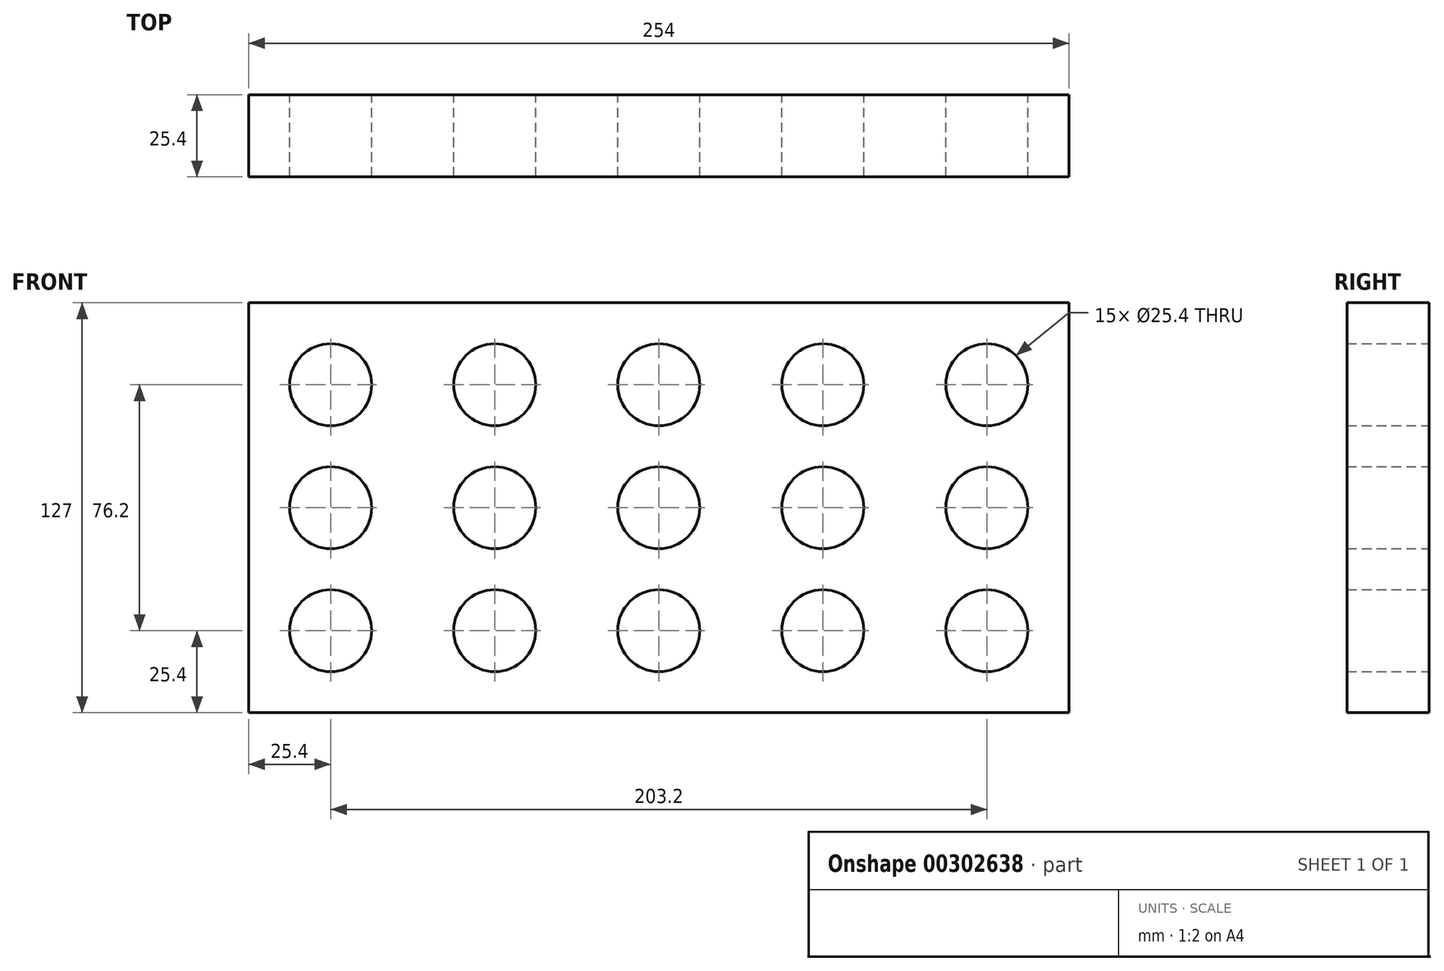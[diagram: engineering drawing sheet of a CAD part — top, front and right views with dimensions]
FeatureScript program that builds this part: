
annotation { "Feature Type Name" : "Feature", "Feature Type Description" : "" }
export const myFeature = defineFeature(function(context is Context, id is Id, definition is map)
    precondition{}
    {
        {
            var Q0;
            Q0=qCreatedBy(makeId("Front.planeOp"),FACE);
            var sketch = newSketch(context, id + "F0", { "sketchPlane" : qUnion([Q0])});
            skLineSegment(sketch, "E0.bottom", {"start": v(0, 0) * mm, "end": v(254, 0) * mm});
            skLineSegment(sketch, "E0.top", {"start": v(0, -127) * mm, "end": v(254, -127) * mm});
            skLineSegment(sketch, "E0.left", {"start": v(0, 0) * mm, "end": v(0, -127) * mm});
            skLineSegment(sketch, "E0.right", {"start": v(254, 0) * mm, "end": v(254, -127) * mm});
            skCircle(sketch, "E1", {"center": v(25.4, -25.4) * mm, "radius": 12.7 * mm});
            skCircle(sketch, "E2.0.1.0", {"center": v(25.4, -63.5) * mm, "radius": 12.7 * mm});
            skCircle(sketch, "E2.0.2.0", {"center": v(25.4, -101.6) * mm, "radius": 12.7 * mm});
            skCircle(sketch, "E2.1.0.0", {"center": v(76.2, -25.4) * mm, "radius": 12.7 * mm});
            skCircle(sketch, "E2.1.1.0", {"center": v(76.2, -63.5) * mm, "radius": 12.7 * mm});
            skCircle(sketch, "E2.1.2.0", {"center": v(76.2, -101.6) * mm, "radius": 12.7 * mm});
            skCircle(sketch, "E2.2.0.0", {"center": v(127, -25.4) * mm, "radius": 12.7 * mm});
            skCircle(sketch, "E2.2.1.0", {"center": v(127, -63.5) * mm, "radius": 12.7 * mm});
            skCircle(sketch, "E2.2.2.0", {"center": v(127, -101.6) * mm, "radius": 12.7 * mm});
            skCircle(sketch, "E2.3.0.0", {"center": v(177.8, -25.4) * mm, "radius": 12.7 * mm});
            skCircle(sketch, "E2.3.1.0", {"center": v(177.8, -63.5) * mm, "radius": 12.7 * mm});
            skCircle(sketch, "E2.3.2.0", {"center": v(177.8, -101.6) * mm, "radius": 12.7 * mm});
            skCircle(sketch, "E2.4.0.0", {"center": v(228.6, -25.4) * mm, "radius": 12.7 * mm});
            skCircle(sketch, "E2.4.1.0", {"center": v(228.6, -63.5) * mm, "radius": 12.7 * mm});
            skCircle(sketch, "E2.4.2.0", {"center": v(228.6, -101.6) * mm, "radius": 12.7 * mm});
            skLineSegment(sketch, "E2.direction1", {"start": v(25.4, -25.4) * mm, "end": v(76.2, -25.4) * mm, "construction": true});
            skLineSegment(sketch, "E2.direction2", {"start": v(25.4, -25.4) * mm, "end": v(25.4, -63.5) * mm, "construction": true});
            skSolve(sketch);
        }
        {
            var Q0;
            Q0 = qSketchRegion(id + "F0", true);
            extrude(context, id + "F1", {"entities" : qUnion([Q0]), "depth" : 25.4 * mm});
        }
    });
